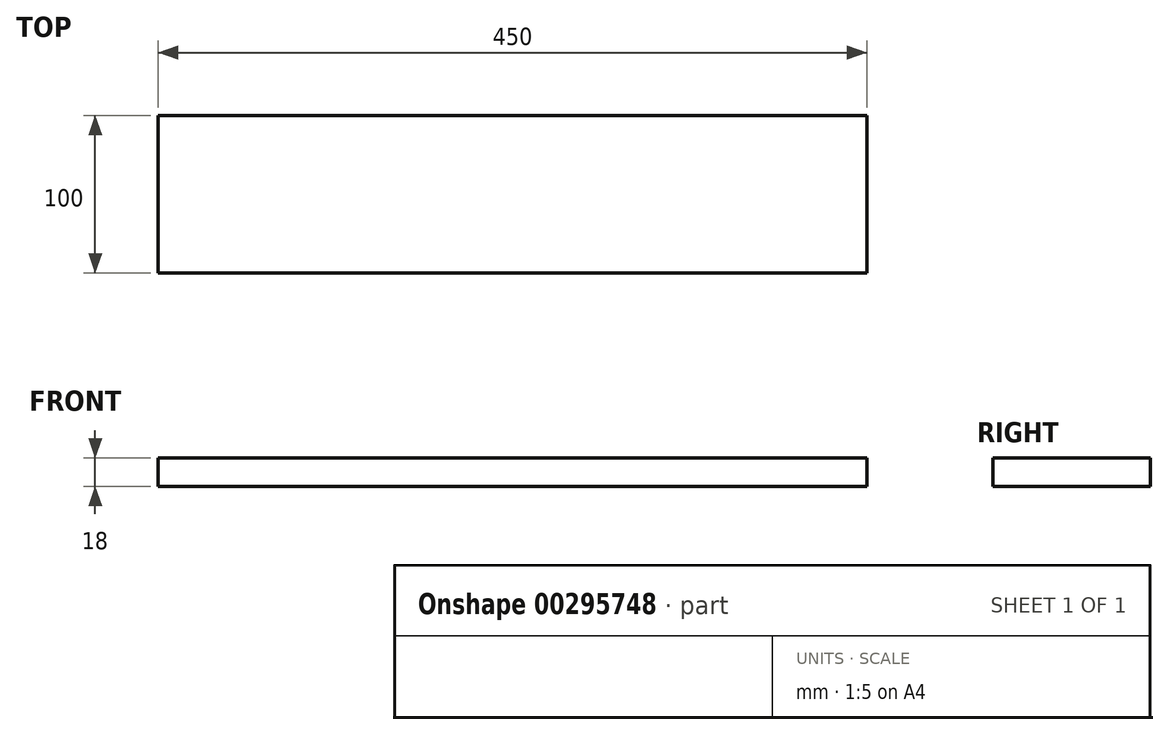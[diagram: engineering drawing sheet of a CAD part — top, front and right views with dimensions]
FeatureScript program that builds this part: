
annotation { "Feature Type Name" : "Feature", "Feature Type Description" : "" }
export const myFeature = defineFeature(function(context is Context, id is Id, definition is map)
    precondition{}
    {
        {
            var Q0;
            Q0=qCreatedBy(makeId("Top.planeOp"),FACE);
            var sketch = newSketch(context, id + "F0", { "sketchPlane" : qUnion([Q0])});
            skLineSegment(sketch, "E0.bottom", {"start": v(-224.73, -11.24) * mm, "end": v(225.27, -11.24) * mm});
            skLineSegment(sketch, "E0.top", {"start": v(-224.73, -111.24) * mm, "end": v(225.27, -111.24) * mm});
            skLineSegment(sketch, "E0.left", {"start": v(-224.73, -11.24) * mm, "end": v(-224.73, -111.24) * mm});
            skLineSegment(sketch, "E0.right", {"start": v(225.27, -11.24) * mm, "end": v(225.27, -111.24) * mm});
            skSolve(sketch);
        }
        {
            var Q0;
            Q0 = qSketchRegion(id + "F0", true);
            extrude(context, id + "F1", {"entities" : qUnion([Q0]), "depth" : 18 * mm});
        }
    });
